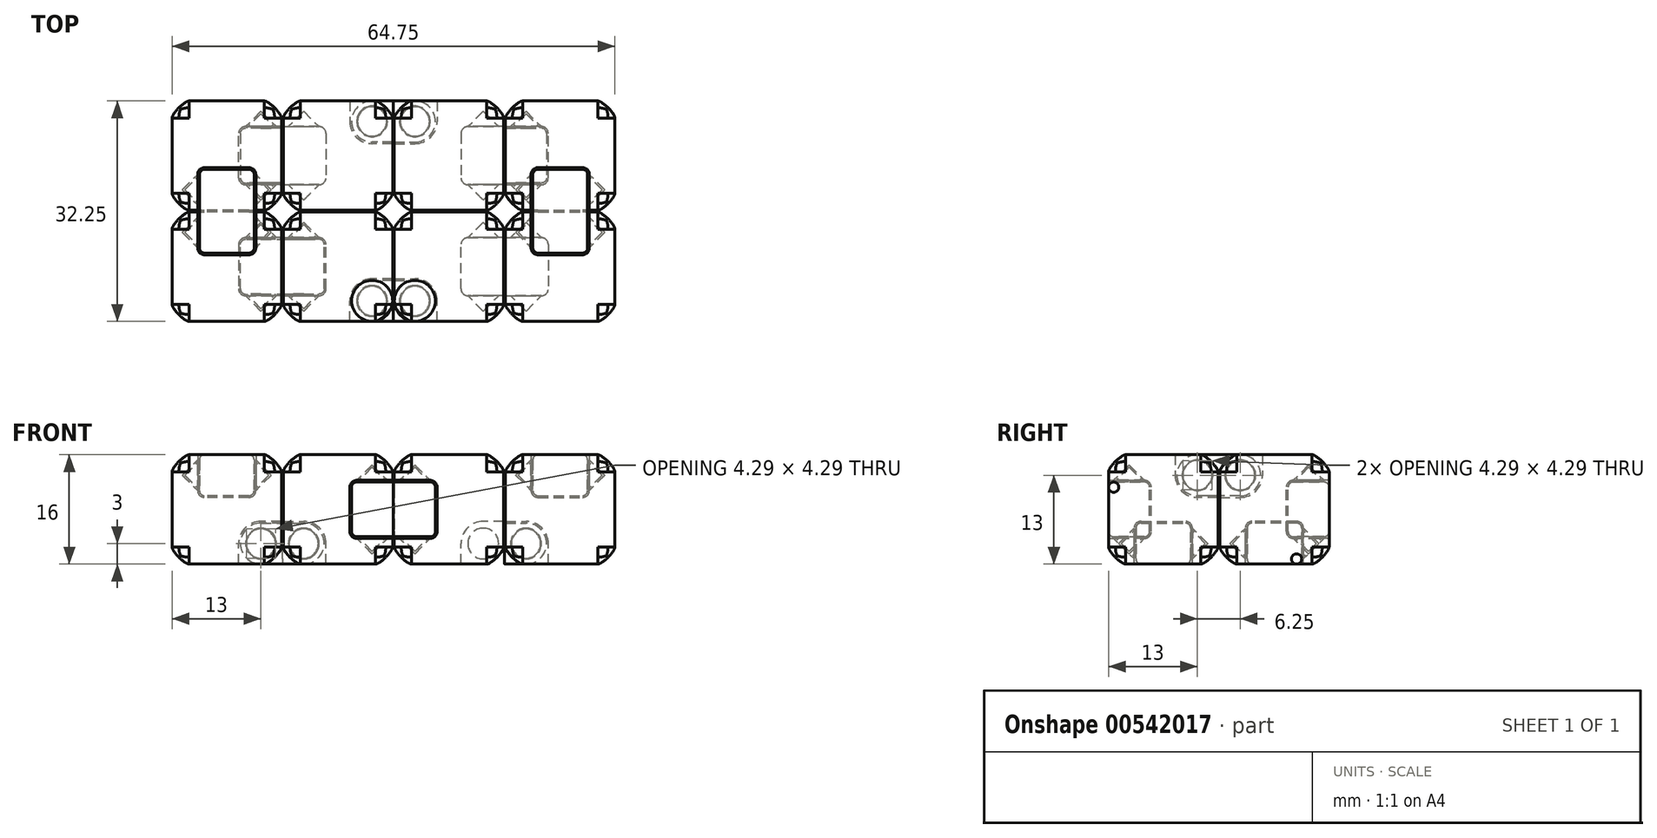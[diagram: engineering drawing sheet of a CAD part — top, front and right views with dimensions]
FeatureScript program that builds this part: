
annotation { "Feature Type Name" : "Feature", "Feature Type Description" : "" }
export const myFeature = defineFeature(function(context is Context, id is Id, definition is map)
    precondition{}
    {
        {
            assignVariable(context, id + "F0", {"name" : "cubeSize", "anyValue" : 16});
        }
        {
            assignVariable(context, id + "F1", {"name" : "hingeSize", "anyValue" : getVariable(context, 'cubeSize') / 2});
        }
        {
            assignVariable(context, id + "F2", {"name" : "hingeDiameter", "anyValue" : getVariable(context, 'hingeSize') / 2});
        }
        {
            assignVariable(context, id + "F3", {"name" : "minThickness", "anyValue" : 1});
        }
        {
            assignVariable(context, id + "F4", {"name" : "hingeGap", "anyValue" : .25});
        }
        {
            var Q0;
            Q0=qCreatedBy(makeId("Top.planeOp"),FACE);
            var sketch = newSketch(context, id + "F5", { "sketchPlane" : qUnion([Q0])});
            skLineSegment(sketch, "E0.bottom", {"start": v(8, -8) * mm, "end": v(-8, -8) * mm});
            skLineSegment(sketch, "E0.top", {"start": v(8, 8) * mm, "end": v(-8, 8) * mm});
            skLineSegment(sketch, "E0.left", {"start": v(8, -8) * mm, "end": v(8, 8) * mm});
            skLineSegment(sketch, "E0.right", {"start": v(-8, -8) * mm, "end": v(-8, 8) * mm});
            skPoint(sketch, "E0.middle", {"position": v(0, 0) * mm});
            skSolve(sketch);
        }
        {
            var Q0;
            Q0=qSketchRegion(id+"F5",true);
            extrude(context, id + "F6", {"entities" : qUnion([Q0]), "depth" : (getVariable(context, 'cubeSize')) * mm, "offsetDistance" : 25 * mm});
        }
        {
            var Q0;
            Q0=qCreatedBy(makeId("Front.planeOp"),FACE);
            var sketch = newSketch(context, id + "F7", { "sketchPlane" : qUnion([Q0])});
            skCircle(sketch, "E1", {"center": v(5, 3) * mm, "radius": 2 * mm});
            skLineSegment(sketch, "E2", {"start": v(5, 3) * mm, "end": v(7, 3) * mm, "construction": true});
            skLineSegment(sketch, "E3", {"start": v(7, 3) * mm, "end": v(8, 3) * mm, "construction": true});
            skLineSegment(sketch, "E4", {"start": v(5, 0) * mm, "end": v(5, 1) * mm, "construction": true});
            skLineSegment(sketch, "E5", {"start": v(5, 1) * mm, "end": v(5, 3) * mm, "construction": true});
            skLineSegment(sketch, "E6", {"start": v(8, 0) * mm, "end": v(1.75, 0) * mm});
            skLineSegment(sketch, "E7", {"start": v(1.75, 0) * mm, "end": v(1.75, 3) * mm});
            skLineSegment(sketch, "E8", {"start": v(8, 0) * mm, "end": v(8, 6.25) * mm});
            skLineSegment(sketch, "E9", {"start": v(8, 6.25) * mm, "end": v(5, 6.25) * mm});
            skArc(sketch, "E10", {"start": v(5, 6.25) * mm, "mid": v(2.7, 5.3) * mm, "end": v(1.75, 3) * mm});
            skSolve(sketch);
        }
        {
            var Q0;
            Q0=makeQuery(id+"F7.imprint","IMPRINT",FACE,{"disambiguationData":[TD([[makeQuery(id+"F7.imprint","IMPRINT",EDGE,{"derivedFrom":sQuery(id+"F7.wireOp",EDGE,"E1")}),-1.0]])]});
            var Q1;
            Q1=makeQuery(id+"F7.imprint","IMPRINT",FACE,{"disambiguationData":[TD([[makeQuery(id+"F7.imprint","IMPRINT",EDGE,{"derivedFrom":sQuery(id+"F7.wireOp",EDGE,"E1")}),1.0]])]});
            extrude(context, id + "F8", {"entities" : qUnion([Q0, Q1]), "operationType" : NewBodyOperationType.REMOVE, "oppositeDirection" : true, "depth" : (getVariable(context, 'hingeSize') + getVariable(context, 'hingeGap') * 2) * mm, "offsetDistance" : 25 * mm, "symmetric" : true});
        }
        {
            var Q0;
            Q0=makeQuery(id+"F6.opExtrude","CAP_VERTEX",VERTEX,{"disambiguationData":[OSD([sQuery(id+"F5.wireOp",EDGE,"E0.bottom"),sQuery(id+"F5.wireOp",EDGE,"E0.right")])],"isStart":false});
            var Q1;
            Q1=makeQuery(id+"F6.opExtrude","CAP_VERTEX",VERTEX,{"disambiguationData":[OSD([sQuery(id+"F5.wireOp",EDGE,"E0.bottom"),sQuery(id+"F5.wireOp",EDGE,"E0.left")])],"isStart":true});
            var Q2;
            Q2=makeQuery(id+"F6.opExtrude","CAP_VERTEX",VERTEX,{"disambiguationData":[OSD([sQuery(id+"F5.wireOp",EDGE,"E0.top"),sQuery(id+"F5.wireOp",EDGE,"E0.left")])],"isStart":true});
            cPlane(context, id + "F9", {"entities" : qUnion([Q0, Q1, Q2]), "cplaneType" : CPlaneType.THREE_POINT, "offset" : 25 * mm, "width" : 150 * mm, "height" : 150 * mm});
        }
        {
            var Q0;
            Q0=qCreatedBy(id+"F9.planeOp",FACE);
            var sketch = newSketch(context, id + "F10", { "sketchPlane" : qUnion([Q0])});
            skLineSegment(sketch, "E11", {"start": v(4.25, 0.84) * mm, "end": v(-4.25, 0.84) * mm});
            skLineSegment(sketch, "E12", {"start": v(-4.25, 0.84) * mm, "end": v(-6.5, -1.41) * mm});
            skLineSegment(sketch, "E13", {"start": v(-6.5, -1.41) * mm, "end": v(6.5, -1.41) * mm});
            skLineSegment(sketch, "E14", {"start": v(6.5, -1.41) * mm, "end": v(4.25, 0.84) * mm});
            skSolve(sketch);
        }
        {
            var Q0;
            Q0=makeQuery(id+"F10.imprint","IMPRINT",FACE,{"disambiguationData":[TD([[makeQuery(id+"F10.imprint","IMPRINT",EDGE,{"derivedFrom":sQuery(id+"F10.wireOp",EDGE,"E11")}),1.0]])]});
            var Q1;
            Q1=sQuery(id+"F10.wireOp",EDGE,"E13");
            revolve(context, id + "F11", {"operationType" : NewBodyOperationType.REMOVE, "entities" : qUnion([Q0]), "axis" : qUnion([Q1]), "revolveType" : RevolveType.FULL, "oppositeDirection" : true});
        }
        {
            var Q0;
            Q0=qCreatedBy(makeId("Right.planeOp"),FACE);
            var sketch = newSketch(context, id + "F12", { "sketchPlane" : qUnion([Q0])});
            skCircle(sketch, "E15", {"center": v(5, 13) * mm, "radius": 2 * mm});
            skLineSegment(sketch, "E16", {"start": v(1.75, 16) * mm, "end": v(8, 16) * mm});
            skLineSegment(sketch, "E17", {"start": v(8, 16) * mm, "end": v(8, 9.75) * mm});
            skLineSegment(sketch, "E18", {"start": v(8, 9.75) * mm, "end": v(5, 9.75) * mm});
            skLineSegment(sketch, "E19", {"start": v(1.75, 16) * mm, "end": v(1.75, 13) * mm});
            skLineSegment(sketch, "E20", {"start": v(5, 13) * mm, "end": v(7, 13) * mm, "construction": true});
            skLineSegment(sketch, "E21", {"start": v(7, 13) * mm, "end": v(8, 13) * mm, "construction": true});
            skLineSegment(sketch, "E22", {"start": v(5, 13) * mm, "end": v(5, 15) * mm, "construction": true});
            skLineSegment(sketch, "E23", {"start": v(5, 15) * mm, "end": v(5, 16) * mm, "construction": true});
            skArc(sketch, "E24", {"start": v(1.75, 13) * mm, "mid": v(2.7, 10.7) * mm, "end": v(5, 9.75) * mm});
            skSolve(sketch);
        }
        {
            var Q0;
            Q0=makeQuery(id+"F12.imprint","IMPRINT",FACE,{"disambiguationData":[TD([[makeQuery(id+"F12.imprint","IMPRINT",EDGE,{"derivedFrom":sQuery(id+"F12.wireOp",EDGE,"E15")}),1.0]])]});
            var Q1;
            Q1=makeQuery(id+"F12.imprint","IMPRINT",FACE,{"disambiguationData":[TD([[makeQuery(id+"F12.imprint","IMPRINT",EDGE,{"derivedFrom":sQuery(id+"F12.wireOp",EDGE,"E15")}),-1.0]])]});
            extrude(context, id + "F13", {"entities" : qUnion([Q0, Q1]), "operationType" : NewBodyOperationType.REMOVE, "depth" : (getVariable(context, 'hingeSize') + getVariable(context, 'hingeGap') * 2) * mm, "offsetDistance" : 25 * mm, "symmetric" : true});
        }
        {
            var Q0;
            Q0=makeQuery(id+"F6.opExtrude","CAP_VERTEX",VERTEX,{"disambiguationData":[OSD([sQuery(id+"F5.wireOp",EDGE,"E0.top"),sQuery(id+"F5.wireOp",EDGE,"E0.left")])],"isStart":false});
            var Q1;
            Q1=makeQuery(id+"F6.opExtrude","CAP_VERTEX",VERTEX,{"disambiguationData":[OSD([sQuery(id+"F5.wireOp",EDGE,"E0.top"),sQuery(id+"F5.wireOp",EDGE,"E0.right")])],"isStart":false});
            var Q2;
            Q2=makeQuery(id+"F6.opExtrude","CAP_VERTEX",VERTEX,{"disambiguationData":[OSD([sQuery(id+"F5.wireOp",EDGE,"E0.bottom"),sQuery(id+"F5.wireOp",EDGE,"E0.right")])],"isStart":true});
            cPlane(context, id + "F14", {"entities" : qUnion([Q0, Q1, Q2]), "cplaneType" : CPlaneType.THREE_POINT, "offset" : 25 * mm, "width" : 150 * mm, "height" : 150 * mm});
        }
        {
            var Q0;
            Q0=qCreatedBy(id+"F14.planeOp",FACE);
            var sketch = newSketch(context, id + "F15", { "sketchPlane" : qUnion([Q0])});
            skLineSegment(sketch, "E25", {"start": v(-6.5, 12.73) * mm, "end": v(6.5, 12.73) * mm});
            skLineSegment(sketch, "E26", {"start": v(6.5, 12.73) * mm, "end": v(4.25, 10.48) * mm});
            skLineSegment(sketch, "E27", {"start": v(4.25, 10.48) * mm, "end": v(-4.25, 10.48) * mm});
            skLineSegment(sketch, "E28", {"start": v(-4.25, 10.48) * mm, "end": v(-6.5, 12.73) * mm});
            skSolve(sketch);
        }
        {
            var Q0;
            Q0 = qSketchRegion(id + "F15", true);
            var Q1;
            Q1=sQuery(id+"F15.wireOp",EDGE,"E25");
            revolve(context, id + "F16", {"operationType" : NewBodyOperationType.REMOVE, "entities" : qUnion([Q0]), "axis" : qUnion([Q1]), "revolveType" : RevolveType.FULL, "oppositeDirection" : true});
        }
        {
            var Q0;
            Q0=makeQuery(id+"F6.opExtrude","SWEPT_FACE",FACE,{"disambiguationData":[OSD([sQuery(id+"F5.wireOp",EDGE,"E0.right")])]});
            var Q1;
            Q1=makeQuery(id+"F6.opExtrude","SWEPT_FACE",FACE,{"disambiguationData":[OSD([sQuery(id+"F5.wireOp",EDGE,"E0.bottom")])]});
            var Q2;
            {var subQ0=sQuery(id+"F5.wireOp",EDGE,"E0.right");var subQ1=sQuery(id+"F5.wireOp",EDGE,"E0.top");Q2=makeQuery(id+"F13.boolean.opBoolean","SPLIT",EDGE,{"disambiguationData":[TD([makeQuery(id+"F6.opExtrude","SWEPT_FACE",FACE,{"disambiguationData":[OSD([subQ0])]})])],"derivedFrom":makeQuery(id+"F6.opExtrude","CAP_EDGE",EDGE,{"disambiguationData":[OSD([subQ1])],"isStart":false})});}
            var Q3;
            {var subQ0=sQuery(id+"F5.wireOp",EDGE,"E0.left");var subQ1=sQuery(id+"F5.wireOp",EDGE,"E0.top");Q3=makeQuery(id+"F13.boolean.opBoolean","SPLIT",EDGE,{"disambiguationData":[TD([makeQuery(id+"F6.opExtrude","SWEPT_FACE",FACE,{"disambiguationData":[OSD([subQ0])]})])],"derivedFrom":makeQuery(id+"F6.opExtrude","CAP_EDGE",EDGE,{"disambiguationData":[OSD([subQ1])],"isStart":false})});}
            var Q4;
            Q4=makeQuery(id+"F6.opExtrude","CAP_EDGE",EDGE,{"disambiguationData":[OSD([sQuery(id+"F5.wireOp",EDGE,"E0.left")])],"isStart":false});
            var Q5;
            Q5=makeQuery(id+"F6.opExtrude","SWEPT_EDGE",EDGE,{"disambiguationData":[OSD([sQuery(id+"F5.wireOp",EDGE,"E0.top"),sQuery(id+"F5.wireOp",EDGE,"E0.left")])]});
            var Q6;
            {var subQ0=sQuery(id+"F5.wireOp",EDGE,"E0.left");var subQ1=sQuery(id+"F5.wireOp",EDGE,"E0.top");Q6=makeQuery(id+"F8.boolean.opBoolean","SPLIT",EDGE,{"disambiguationData":[TD([makeQuery(id+"F6.opExtrude","SWEPT_FACE",FACE,{"disambiguationData":[OSD([subQ1])]})])],"derivedFrom":makeQuery(id+"F6.opExtrude","CAP_EDGE",EDGE,{"disambiguationData":[OSD([subQ0])],"isStart":true})});}
            var Q7;
            Q7=makeQuery(id+"F6.opExtrude","CAP_EDGE",EDGE,{"disambiguationData":[OSD([sQuery(id+"F5.wireOp",EDGE,"E0.top")])],"isStart":true});
            var Q8;
            {var subQ0=sQuery(id+"F5.wireOp",EDGE,"E0.bottom");var subQ1=sQuery(id+"F5.wireOp",EDGE,"E0.left");Q8=makeQuery(id+"F8.boolean.opBoolean","SPLIT",EDGE,{"disambiguationData":[TD([makeQuery(id+"F6.opExtrude","SWEPT_FACE",FACE,{"disambiguationData":[OSD([subQ0])]})])],"derivedFrom":makeQuery(id+"F6.opExtrude","CAP_EDGE",EDGE,{"disambiguationData":[OSD([subQ1])],"isStart":true})});}
            fillet(context, id + "F17", {"entities" : qUnion([Q0, Q1, Q2, Q3, Q4, Q5, Q6, Q7, Q8]), "radius" : (getVariable(context, 'hingeDiameter') / 2 + getVariable(context, 'minThickness') - .5) * mm, "tangentPropagation" : true, "rho" : .2, "crossSection" : FilletCrossSection.CONIC, "allowEdgeOverflow" : false});
        }
        {
            var Q0;
            Q0=makeQuery(id+"F8.boolean.opBoolean","COPY",EDGE,{"derivedFrom":makeQuery(id+"F8.opExtrude","CAP_EDGE",EDGE,{"disambiguationData":[OSD([sQuery(id+"F7.wireOp",EDGE,"E7")])],"isStart":true})});
            var Q1;
            Q1=makeQuery(id+"F8.boolean.opBoolean","COPY",EDGE,{"derivedFrom":makeQuery(id+"F8.opExtrude","CAP_EDGE",EDGE,{"disambiguationData":[OSD([sQuery(id+"F7.wireOp",EDGE,"E7")])],"isStart":false})});
            var Q2;
            Q2=makeQuery(id+"F13.boolean.opBoolean","COPY",EDGE,{"derivedFrom":makeQuery(id+"F13.opExtrude","CAP_EDGE",EDGE,{"disambiguationData":[OSD([sQuery(id+"F12.wireOp",EDGE,"E18")])],"isStart":false})});
            var Q3;
            Q3=makeQuery(id+"F13.boolean.opBoolean","COPY",EDGE,{"derivedFrom":makeQuery(id+"F13.opExtrude","CAP_EDGE",EDGE,{"disambiguationData":[OSD([sQuery(id+"F12.wireOp",EDGE,"E18")])],"isStart":true})});
            fillet(context, id + "F18", {"entities" : qUnion([Q0, Q1, Q2, Q3]), "radius" : (getVariable(context, 'minThickness')) * mm, "tangentPropagation" : true, "allowEdgeOverflow" : false});
        }
        {
            var Q0;
            Q0=qCreatedBy(makeId("Front.planeOp"),FACE);
            var sketch = newSketch(context, id + "F19", { "sketchPlane" : qUnion([Q0])});
            skCircle(sketch, "E29", {"center": v(5, 3) * mm, "radius": 2 * mm, "construction": true});
            skArc(sketch, "E30", {"start": v(5, 6) * mm, "mid": v(2, 3) * mm, "end": v(5, 0) * mm});
            skArc(sketch, "E31", {"start": v(11.25, 0) * mm, "mid": v(14.25, 3) * mm, "end": v(11.25, 6) * mm});
            skLineSegment(sketch, "E32", {"start": v(5, 3) * mm, "end": v(8, 3) * mm, "construction": true});
            skCircle(sketch, "E33", {"center": v(11.25, 3) * mm, "radius": 2 * mm, "construction": true});
            skLineSegment(sketch, "E34", {"start": v(8, 3) * mm, "end": v(8.25, 3) * mm, "construction": true});
            skLineSegment(sketch, "E35", {"start": v(8.25, 3) * mm, "end": v(11.25, 3) * mm, "construction": true});
            skLineSegment(sketch, "E36", {"start": v(8.12, 0) * mm, "end": v(8.12, 3) * mm});
            skLineSegment(sketch, "E37", {"start": v(8.12, 3) * mm, "end": v(8.12, 6) * mm});
            skLineSegment(sketch, "E38", {"start": v(11.25, 0) * mm, "end": v(5, 0) * mm});
            skLineSegment(sketch, "E39", {"start": v(11.25, 6) * mm, "end": v(5, 6) * mm});
            skSolve(sketch);
        }
        {
            var Q0;
            Q0=makeQuery(id+"F19.imprint","IMPRINT",FACE,{"disambiguationData":[TD([[makeQuery(id+"F19.imprint","IMPRINT",EDGE,{"derivedFrom":sQuery(id+"F19.wireOp",EDGE,"E30")}),1.0]])]});
            extrude(context, id + "F20", {"entities" : qUnion([Q0]), "depth" : (getVariable(context, 'hingeSize')) * mm, "offsetDistance" : 25 * mm, "symmetric" : true});
        }
        {
            var Q0;
            Q0=qCreatedBy(id+"F9.planeOp",FACE);
            var sketch = newSketch(context, id + "F21", { "sketchPlane" : qUnion([Q0])});
            skLineSegment(sketch, "E40", {"start": v(6.15, -1.41) * mm, "end": v(3.9, 0.84) * mm});
            skLineSegment(sketch, "E41", {"start": v(3.9, 0.84) * mm, "end": v(-3.9, 0.84) * mm});
            skLineSegment(sketch, "E42", {"start": v(-3.9, 0.84) * mm, "end": v(-6.15, -1.41) * mm});
            skLineSegment(sketch, "E43", {"start": v(-6.15, -1.41) * mm, "end": v(6.15, -1.41) * mm});
            skSolve(sketch);
        }
        {
            var Q0;
            Q0 = qSketchRegion(id + "F21", true);
            var Q1;
            Q1=sQuery(id+"F21.wireOp",EDGE,"E43");
            revolve(context, id + "F22", {"operationType" : NewBodyOperationType.ADD, "entities" : qUnion([Q0]), "axis" : qUnion([Q1]), "revolveType" : RevolveType.FULL});
        }
        {
            var Q0;
            Q0=qCreatedBy(makeId("Right.planeOp"),FACE);
            var sketch = newSketch(context, id + "F23", { "sketchPlane" : qUnion([Q0])});
            skCircle(sketch, "E44", {"center": v(5, 13) * mm, "radius": 2.25 * mm, "construction": true});
            skArc(sketch, "E45", {"start": v(5, 16) * mm, "mid": v(2, 13) * mm, "end": v(5, 10) * mm});
            skArc(sketch, "E46", {"start": v(11.25, 10) * mm, "mid": v(14.25, 13) * mm, "end": v(11.25, 16) * mm});
            skLineSegment(sketch, "E47", {"start": v(5, 13) * mm, "end": v(8, 13) * mm, "construction": true});
            skCircle(sketch, "E48", {"center": v(11.25, 13) * mm, "radius": 2 * mm, "construction": true});
            skLineSegment(sketch, "E49", {"start": v(8, 13) * mm, "end": v(8.25, 13) * mm, "construction": true});
            skLineSegment(sketch, "E50", {"start": v(8.25, 13) * mm, "end": v(11.25, 13) * mm, "construction": true});
            skLineSegment(sketch, "E51", {"start": v(8.12, 10) * mm, "end": v(8.12, 13) * mm});
            skLineSegment(sketch, "E52", {"start": v(8.12, 13) * mm, "end": v(8.12, 16) * mm});
            skLineSegment(sketch, "E53", {"start": v(11.25, 10) * mm, "end": v(5, 10) * mm});
            skLineSegment(sketch, "E54", {"start": v(11.25, 16) * mm, "end": v(5, 16) * mm});
            skSolve(sketch);
        }
        {
            var Q0;
            {var subQ3=sQuery(id+"F23.wireOp",EDGE,"E45");Q0=makeQuery(id+"F23.imprint","IMPRINT",FACE,{"disambiguationData":[TD([[makeQuery(id+"F23.imprint","IMPRINT",EDGE,{"derivedFrom":subQ3}),1.0]])]});}
            extrude(context, id + "F24", {"entities" : qUnion([Q0]), "depth" : (getVariable(context, 'hingeSize')) * mm, "offsetDistance" : 25 * mm, "symmetric" : true});
        }
        {
            var Q0;
            Q0=makeQuery(id+"F20.opExtrude","CAP_EDGE",EDGE,{"disambiguationData":[OSD([sQuery(id+"F19.wireOp",EDGE,"E38")])],"isStart":false});
            var Q1;
            Q1=makeQuery(id+"F20.opExtrude","CAP_EDGE",EDGE,{"disambiguationData":[OSD([sQuery(id+"F19.wireOp",EDGE,"E38")])],"isStart":true});
            var Q2;
            Q2=makeQuery(id+"F24.opExtrude","CAP_EDGE",EDGE,{"disambiguationData":[OSD([sQuery(id+"F23.wireOp",EDGE,"E54")])],"isStart":false});
            var Q3;
            Q3=makeQuery(id+"F24.opExtrude","CAP_EDGE",EDGE,{"disambiguationData":[OSD([sQuery(id+"F23.wireOp",EDGE,"E54")])],"isStart":true});
            fillet(context, id + "F25", {"entities" : qUnion([Q0, Q1, Q2, Q3]), "radius" : (getVariable(context, 'minThickness') - getVariable(context, 'hingeGap')) * mm, "tangentPropagation" : true, "allowEdgeOverflow" : false});
        }
        {
            var Q0;
            Q0=qCreatedBy(id+"F14.planeOp",FACE);
            var sketch = newSketch(context, id + "F26", { "sketchPlane" : qUnion([Q0])});
            skLineSegment(sketch, "E55", {"start": v(-6.15, 12.73) * mm, "end": v(6.15, 12.73) * mm});
            skLineSegment(sketch, "E56", {"start": v(6.15, 12.73) * mm, "end": v(3.9, 10.48) * mm});
            skLineSegment(sketch, "E57", {"start": v(3.9, 10.48) * mm, "end": v(-3.9, 10.48) * mm});
            skLineSegment(sketch, "E58", {"start": v(-3.9, 10.48) * mm, "end": v(-6.15, 12.73) * mm});
            skSolve(sketch);
        }
        {
            var Q0;
            Q0=makeQuery(id+"F26.imprint","IMPRINT",FACE,{"disambiguationData":[TD([[makeQuery(id+"F26.imprint","IMPRINT",EDGE,{"derivedFrom":sQuery(id+"F26.wireOp",EDGE,"E55")}),-1.0]])]});
            var Q1;
            Q1=sQuery(id+"F26.wireOp",EDGE,"E55");
            revolve(context, id + "F27", {"operationType" : NewBodyOperationType.ADD, "entities" : qUnion([Q0]), "axis" : qUnion([Q1]), "revolveType" : RevolveType.FULL});
        }
        {
            var Q0;
            Q0=makeQuery(id+"F20.opExtrude","SWEPT_FACE",FACE,{"disambiguationData":[OSD([sQuery(id+"F19.wireOp",EDGE,"E36"),sQuery(id+"F19.wireOp",EDGE,"E37")])]});
            var sketch = newSketch(context, id + "F28", { "sketchPlane" : qUnion([Q0])});
            skLineSegment(sketch, "E59", {"start": v(-7.63, -0.12) * mm, "end": v(6.67, -0.12) * mm, "construction": true});
            skSolve(sketch);
        }
        {
            var Q0;
            Q0=makeQuery(id+"F6.opExtrude","SWEPT_BODY",BODY,{"disambiguationData":[OSD([sQuery(id+"F5.wireOp",EDGE,"E0.bottom"),sQuery(id+"F5.wireOp",EDGE,"E0.top"),sQuery(id+"F5.wireOp",EDGE,"E0.left"),sQuery(id+"F5.wireOp",EDGE,"E0.right")])]});
            var Q1;
            Q1=makeQuery(id+"F24.opExtrude","SWEPT_BODY",BODY,{"disambiguationData":[OSD([sQuery(id+"F23.wireOp",EDGE,"E45"),sQuery(id+"F23.wireOp",EDGE,"E51"),sQuery(id+"F23.wireOp",EDGE,"E52"),sQuery(id+"F23.wireOp",EDGE,"E53"),sQuery(id+"F23.wireOp",EDGE,"E54")])]});
            var Q2;
            Q2=sQuery(id+"F28.wireOp",EDGE,"E59");
            circularPattern(context, id + "F29", {"entities" : qUnion([Q0, Q1]), "axis" : qUnion([Q2]), "angle" : 90 * degree, "instanceCount" : 2});
        }
        {
            var Q0;
            Q0=makeQuery(id+"F29.opPattern","COPY",BODY,{"derivedFrom":makeQuery(id+"F6.opExtrude","SWEPT_BODY",BODY,{"disambiguationData":[OSD([sQuery(id+"F5.wireOp",EDGE,"E0.bottom"),sQuery(id+"F5.wireOp",EDGE,"E0.top"),sQuery(id+"F5.wireOp",EDGE,"E0.left"),sQuery(id+"F5.wireOp",EDGE,"E0.right")])]}),"instanceName":"1"});
            var Q1;
            Q1=makeQuery(id+"F29.opPattern","COPY",BODY,{"derivedFrom":makeQuery(id+"F24.opExtrude","SWEPT_BODY",BODY,{"disambiguationData":[OSD([sQuery(id+"F23.wireOp",EDGE,"E45"),sQuery(id+"F23.wireOp",EDGE,"E51"),sQuery(id+"F23.wireOp",EDGE,"E52"),sQuery(id+"F23.wireOp",EDGE,"E53"),sQuery(id+"F23.wireOp",EDGE,"E54")])]}),"instanceName":"1"});
            var Q2;
            Q2=qCreatedBy(makeId("Front.planeOp"),FACE);
            mirror(context, id + "F30", {"entities" : qUnion([Q0, Q1]), "mirrorPlane" : qUnion([Q2])});
        }
        {
            var Q0;
            Q0=makeQuery(id+"F29.opPattern","COPY",BODY,{"derivedFrom":makeQuery(id+"F24.opExtrude","SWEPT_BODY",BODY,{"disambiguationData":[OSD([sQuery(id+"F23.wireOp",EDGE,"E45"),sQuery(id+"F23.wireOp",EDGE,"E51"),sQuery(id+"F23.wireOp",EDGE,"E52"),sQuery(id+"F23.wireOp",EDGE,"E53"),sQuery(id+"F23.wireOp",EDGE,"E54")])]}),"instanceName":"1"});
            var Q1;
            Q1=makeQuery(id+"F29.opPattern","COPY",BODY,{"derivedFrom":makeQuery(id+"F6.opExtrude","SWEPT_BODY",BODY,{"disambiguationData":[OSD([sQuery(id+"F5.wireOp",EDGE,"E0.bottom"),sQuery(id+"F5.wireOp",EDGE,"E0.top"),sQuery(id+"F5.wireOp",EDGE,"E0.left"),sQuery(id+"F5.wireOp",EDGE,"E0.right")])]}),"instanceName":"1"});
            deleteBodies(context, id + "F31", {"entities" : qUnion([Q0, Q1])});
        }
        {
            var Q0;
            Q0=makeQuery(id+"F20.opExtrude","SWEPT_BODY",BODY,{"disambiguationData":[OSD([sQuery(id+"F19.wireOp",EDGE,"E30"),sQuery(id+"F19.wireOp",EDGE,"E36"),sQuery(id+"F19.wireOp",EDGE,"E37"),sQuery(id+"F19.wireOp",EDGE,"E38"),sQuery(id+"F19.wireOp",EDGE,"E39")])]});
            var Q1;
            Q1=makeQuery(id+"F20.opExtrude","SWEPT_FACE",FACE,{"disambiguationData":[OSD([sQuery(id+"F19.wireOp",EDGE,"E36"),sQuery(id+"F19.wireOp",EDGE,"E37")])]});
            mirror(context, id + "F32", {"operationType" : NewBodyOperationType.ADD, "entities" : qUnion([Q0]), "mirrorPlane" : qUnion([Q1])});
        }
        {
            var Q0;
            {var subQ0=sQuery(id+"F5.wireOp",EDGE,"E0.left");var subQ1=makeQuery(id+"F6.opExtrude","SWEPT_FACE",FACE,{"disambiguationData":[OSD([subQ0])]});var subQ2=sQuery(id+"F5.wireOp",EDGE,"E0.bottom");Q0=makeQuery(id+"F30.opPattern","COPY",VERTEX,{"derivedFrom":makeQuery(id+"F29.opPattern","COPY",VERTEX,{"derivedFrom":makeQuery(id+"F17.opFillet","BLEND_VERTEX",VERTEX,{"blendedFrom":[makeQuery(id+"F6.opExtrude","CAP_VERTEX",VERTEX,{"disambiguationData":[OSD([subQ2,subQ0])],"isStart":true}),makeQuery(id+"F6.opExtrude","SWEPT_EDGE",EDGE,{"disambiguationData":[OSD([subQ2,subQ0])]}),makeQuery(id+"F8.boolean.opBoolean","SPLIT",EDGE,{"disambiguationData":[TD([makeQuery(id+"F6.opExtrude","SWEPT_FACE",FACE,{"disambiguationData":[OSD([subQ2])]})])],"derivedFrom":makeQuery(id+"F6.opExtrude","CAP_EDGE",EDGE,{"disambiguationData":[OSD([subQ0])],"isStart":true})}),subQ1],"blendedInto":[subQ1]}),"instanceName":"1"}),"instanceName":"1"});}
            var Q1;
            {var subQ0=sQuery(id+"F5.wireOp",EDGE,"E0.left");var subQ1=sQuery(id+"F5.wireOp",EDGE,"E0.top");Q1=makeQuery(id+"F30.opPattern","COPY",VERTEX,{"derivedFrom":makeQuery(id+"F29.opPattern","COPY",VERTEX,{"derivedFrom":makeQuery(id+"F17.opFillet","BLEND_VERTEX",VERTEX,{"blendedFrom":[makeQuery(id+"F6.opExtrude","CAP_VERTEX",VERTEX,{"disambiguationData":[OSD([subQ1,subQ0])],"isStart":false}),makeQuery(id+"F6.opExtrude","SWEPT_EDGE",EDGE,{"disambiguationData":[OSD([subQ1,subQ0])]}),makeQuery(id+"F6.opExtrude","CAP_EDGE",EDGE,{"disambiguationData":[OSD([subQ0])],"isStart":false}),makeQuery(id+"F6.opExtrude","SWEPT_FACE",FACE,{"disambiguationData":[OSD([subQ0])]})],"blendedInto":[makeQuery(id+"F6.opExtrude","SWEPT_FACE",FACE,{"disambiguationData":[OSD([subQ0])]})]}),"instanceName":"1"}),"instanceName":"1"});}
            var Q2;
            {var subQ0=sQuery(id+"F5.wireOp",EDGE,"E0.right");var subQ1=sQuery(id+"F5.wireOp",EDGE,"E0.top");Q2=makeQuery(id+"F30.opPattern","COPY",VERTEX,{"derivedFrom":makeQuery(id+"F29.opPattern","COPY",VERTEX,{"derivedFrom":makeQuery(id+"F17.opFillet","BLEND_VERTEX",VERTEX,{"blendedFrom":[makeQuery(id+"F6.opExtrude","CAP_VERTEX",VERTEX,{"disambiguationData":[OSD([subQ1,subQ0])],"isStart":false}),makeQuery(id+"F6.opExtrude","SWEPT_EDGE",EDGE,{"disambiguationData":[OSD([subQ1,subQ0])]}),makeQuery(id+"F6.opExtrude","CAP_EDGE",EDGE,{"disambiguationData":[OSD([subQ0])],"isStart":false}),makeQuery(id+"F6.opExtrude","SWEPT_FACE",FACE,{"disambiguationData":[OSD([subQ0])]})],"blendedInto":[makeQuery(id+"F6.opExtrude","SWEPT_FACE",FACE,{"disambiguationData":[OSD([subQ0])]})]}),"instanceName":"1"}),"instanceName":"1"});}
            cPlane(context, id + "F33", {"entities" : qUnion([Q0, Q1, Q2]), "cplaneType" : CPlaneType.THREE_POINT, "offset" : 25 * mm, "width" : 150 * mm, "height" : 150 * mm});
        }
        {
            var Q0;
            Q0=qCreatedBy(id+"F33.planeOp",FACE);
            var sketch = newSketch(context, id + "F34", { "sketchPlane" : qUnion([Q0])});
            skLineSegment(sketch, "E60", {"start": v(-18.56, 14.15) * mm, "end": v(-18.56, 1.85) * mm, "construction": true});
            skSolve(sketch);
        }
        {
            var Q0;
            Q0=makeQuery(id+"F30.opPattern","COPY",BODY,{"derivedFrom":makeQuery(id+"F29.opPattern","COPY",BODY,{"derivedFrom":makeQuery(id+"F24.opExtrude","SWEPT_BODY",BODY,{"disambiguationData":[OSD([sQuery(id+"F23.wireOp",EDGE,"E45"),sQuery(id+"F23.wireOp",EDGE,"E51"),sQuery(id+"F23.wireOp",EDGE,"E52"),sQuery(id+"F23.wireOp",EDGE,"E53"),sQuery(id+"F23.wireOp",EDGE,"E54")])]}),"instanceName":"1"}),"instanceName":"1"});
            var Q1;
            Q1=sQuery(id+"F34.wireOp",EDGE,"E60");
            circularPattern(context, id + "F35", {"entities" : qUnion([Q0]), "axis" : qUnion([Q1]), "angle" : 90 * degree, "instanceCount" : 2, "oppositeDirection" : true});
        }
        {
            var Q0;
            Q0=makeQuery(id+"F30.opPattern","COPY",BODY,{"derivedFrom":makeQuery(id+"F29.opPattern","COPY",BODY,{"derivedFrom":makeQuery(id+"F24.opExtrude","SWEPT_BODY",BODY,{"disambiguationData":[OSD([sQuery(id+"F23.wireOp",EDGE,"E45"),sQuery(id+"F23.wireOp",EDGE,"E51"),sQuery(id+"F23.wireOp",EDGE,"E52"),sQuery(id+"F23.wireOp",EDGE,"E53"),sQuery(id+"F23.wireOp",EDGE,"E54")])]}),"instanceName":"1"}),"instanceName":"1"});
            deleteBodies(context, id + "F36", {"entities" : qUnion([Q0])});
        }
        {
            var Q0;
            Q0=makeQuery(id+"F24.opExtrude","SWEPT_BODY",BODY,{"disambiguationData":[OSD([sQuery(id+"F23.wireOp",EDGE,"E45"),sQuery(id+"F23.wireOp",EDGE,"E51"),sQuery(id+"F23.wireOp",EDGE,"E52"),sQuery(id+"F23.wireOp",EDGE,"E53"),sQuery(id+"F23.wireOp",EDGE,"E54")])]});
            var Q1;
            Q1=makeQuery(id+"F6.opExtrude","SWEPT_BODY",BODY,{"disambiguationData":[OSD([sQuery(id+"F5.wireOp",EDGE,"E0.bottom"),sQuery(id+"F5.wireOp",EDGE,"E0.top"),sQuery(id+"F5.wireOp",EDGE,"E0.left"),sQuery(id+"F5.wireOp",EDGE,"E0.right")])]});
            var Q2;
            Q2=makeQuery(id+"F20.opExtrude","SWEPT_BODY",BODY,{"disambiguationData":[OSD([sQuery(id+"F19.wireOp",EDGE,"E30"),sQuery(id+"F19.wireOp",EDGE,"E36"),sQuery(id+"F19.wireOp",EDGE,"E37"),sQuery(id+"F19.wireOp",EDGE,"E38"),sQuery(id+"F19.wireOp",EDGE,"E39")])]});
            var Q3;
            Q3=makeQuery(id+"F30.opPattern","COPY",BODY,{"derivedFrom":makeQuery(id+"F29.opPattern","COPY",BODY,{"derivedFrom":makeQuery(id+"F6.opExtrude","SWEPT_BODY",BODY,{"disambiguationData":[OSD([sQuery(id+"F5.wireOp",EDGE,"E0.bottom"),sQuery(id+"F5.wireOp",EDGE,"E0.top"),sQuery(id+"F5.wireOp",EDGE,"E0.left"),sQuery(id+"F5.wireOp",EDGE,"E0.right")])]}),"instanceName":"1"}),"instanceName":"1"});
            var Q4;
            Q4=makeQuery(id+"F35.opPattern","COPY",BODY,{"derivedFrom":makeQuery(id+"F30.opPattern","COPY",BODY,{"derivedFrom":makeQuery(id+"F29.opPattern","COPY",BODY,{"derivedFrom":makeQuery(id+"F24.opExtrude","SWEPT_BODY",BODY,{"disambiguationData":[OSD([sQuery(id+"F23.wireOp",EDGE,"E45"),sQuery(id+"F23.wireOp",EDGE,"E51"),sQuery(id+"F23.wireOp",EDGE,"E52"),sQuery(id+"F23.wireOp",EDGE,"E53"),sQuery(id+"F23.wireOp",EDGE,"E54")])]}),"instanceName":"1"}),"instanceName":"1"}),"instanceName":"1"});
            var Q5;
            Q5=makeQuery(id+"F24.opExtrude","SWEPT_FACE",FACE,{"disambiguationData":[OSD([sQuery(id+"F23.wireOp",EDGE,"E51"),sQuery(id+"F23.wireOp",EDGE,"E52")])]});
            mirror(context, id + "F37", {"operationType" : NewBodyOperationType.ADD, "entities" : qUnion([Q0, Q1, Q2, Q3, Q4]), "mirrorPlane" : qUnion([Q5])});
        }
        {
            var Q0;
            Q0=makeQuery(id+"F35.opPattern","COPY",BODY,{"derivedFrom":makeQuery(id+"F30.opPattern","COPY",BODY,{"derivedFrom":makeQuery(id+"F29.opPattern","COPY",BODY,{"derivedFrom":makeQuery(id+"F24.opExtrude","SWEPT_BODY",BODY,{"disambiguationData":[OSD([sQuery(id+"F23.wireOp",EDGE,"E45"),sQuery(id+"F23.wireOp",EDGE,"E51"),sQuery(id+"F23.wireOp",EDGE,"E52"),sQuery(id+"F23.wireOp",EDGE,"E53"),sQuery(id+"F23.wireOp",EDGE,"E54")])]}),"instanceName":"1"}),"instanceName":"1"}),"instanceName":"1"});
            var Q1;
            Q1=makeQuery(id+"F37.opPattern","COPY",BODY,{"derivedFrom":makeQuery(id+"F35.opPattern","COPY",BODY,{"derivedFrom":makeQuery(id+"F30.opPattern","COPY",BODY,{"derivedFrom":makeQuery(id+"F29.opPattern","COPY",BODY,{"derivedFrom":makeQuery(id+"F24.opExtrude","SWEPT_BODY",BODY,{"disambiguationData":[OSD([sQuery(id+"F23.wireOp",EDGE,"E45"),sQuery(id+"F23.wireOp",EDGE,"E51"),sQuery(id+"F23.wireOp",EDGE,"E52"),sQuery(id+"F23.wireOp",EDGE,"E53"),sQuery(id+"F23.wireOp",EDGE,"E54")])]}),"instanceName":"1"}),"instanceName":"1"}),"instanceName":"1"}),"instanceName":"1"});
            var Q2;
            Q2=makeQuery(id+"F24.opExtrude","SWEPT_BODY",BODY,{"disambiguationData":[OSD([sQuery(id+"F23.wireOp",EDGE,"E45"),sQuery(id+"F23.wireOp",EDGE,"E51"),sQuery(id+"F23.wireOp",EDGE,"E52"),sQuery(id+"F23.wireOp",EDGE,"E53"),sQuery(id+"F23.wireOp",EDGE,"E54")])]});
            var Q3;
            Q3=makeQuery(id+"F37.opPattern","COPY",BODY,{"derivedFrom":makeQuery(id+"F20.opExtrude","SWEPT_BODY",BODY,{"disambiguationData":[OSD([sQuery(id+"F19.wireOp",EDGE,"E30"),sQuery(id+"F19.wireOp",EDGE,"E36"),sQuery(id+"F19.wireOp",EDGE,"E37"),sQuery(id+"F19.wireOp",EDGE,"E38"),sQuery(id+"F19.wireOp",EDGE,"E39")])]}),"instanceName":"1"});
            var Q4;
            Q4=makeQuery(id+"F20.opExtrude","SWEPT_BODY",BODY,{"disambiguationData":[OSD([sQuery(id+"F19.wireOp",EDGE,"E30"),sQuery(id+"F19.wireOp",EDGE,"E36"),sQuery(id+"F19.wireOp",EDGE,"E37"),sQuery(id+"F19.wireOp",EDGE,"E38"),sQuery(id+"F19.wireOp",EDGE,"E39")])]});
            var Q5;
            Q5=makeQuery(id+"F37.opPattern","COPY",BODY,{"derivedFrom":makeQuery(id+"F30.opPattern","COPY",BODY,{"derivedFrom":makeQuery(id+"F29.opPattern","COPY",BODY,{"derivedFrom":makeQuery(id+"F6.opExtrude","SWEPT_BODY",BODY,{"disambiguationData":[OSD([sQuery(id+"F5.wireOp",EDGE,"E0.bottom"),sQuery(id+"F5.wireOp",EDGE,"E0.top"),sQuery(id+"F5.wireOp",EDGE,"E0.left"),sQuery(id+"F5.wireOp",EDGE,"E0.right")])]}),"instanceName":"1"}),"instanceName":"1"}),"instanceName":"1"});
            var Q6;
            Q6=makeQuery(id+"F37.opPattern","COPY",BODY,{"derivedFrom":makeQuery(id+"F6.opExtrude","SWEPT_BODY",BODY,{"disambiguationData":[OSD([sQuery(id+"F5.wireOp",EDGE,"E0.bottom"),sQuery(id+"F5.wireOp",EDGE,"E0.top"),sQuery(id+"F5.wireOp",EDGE,"E0.left"),sQuery(id+"F5.wireOp",EDGE,"E0.right")])]}),"instanceName":"1"});
            var Q7;
            Q7=makeQuery(id+"F6.opExtrude","SWEPT_BODY",BODY,{"disambiguationData":[OSD([sQuery(id+"F5.wireOp",EDGE,"E0.bottom"),sQuery(id+"F5.wireOp",EDGE,"E0.top"),sQuery(id+"F5.wireOp",EDGE,"E0.left"),sQuery(id+"F5.wireOp",EDGE,"E0.right")])]});
            var Q8;
            Q8=makeQuery(id+"F30.opPattern","COPY",BODY,{"derivedFrom":makeQuery(id+"F29.opPattern","COPY",BODY,{"derivedFrom":makeQuery(id+"F6.opExtrude","SWEPT_BODY",BODY,{"disambiguationData":[OSD([sQuery(id+"F5.wireOp",EDGE,"E0.bottom"),sQuery(id+"F5.wireOp",EDGE,"E0.top"),sQuery(id+"F5.wireOp",EDGE,"E0.left"),sQuery(id+"F5.wireOp",EDGE,"E0.right")])]}),"instanceName":"1"}),"instanceName":"1"});
            var Q9;
            Q9=makeQuery(id+"F35.opPattern","COPY",FACE,{"derivedFrom":makeQuery(id+"F30.opPattern","COPY",FACE,{"derivedFrom":makeQuery(id+"F29.opPattern","COPY",FACE,{"derivedFrom":makeQuery(id+"F24.opExtrude","SWEPT_FACE",FACE,{"disambiguationData":[OSD([sQuery(id+"F23.wireOp",EDGE,"E51"),sQuery(id+"F23.wireOp",EDGE,"E52")])]}),"instanceName":"1"}),"instanceName":"1"}),"instanceName":"1"});
            mirror(context, id + "F38", {"operationType" : NewBodyOperationType.ADD, "entities" : qUnion([Q0, Q1, Q2, Q3, Q4, Q5, Q6, Q7, Q8]), "mirrorPlane" : qUnion([Q9])});
        }
    });
